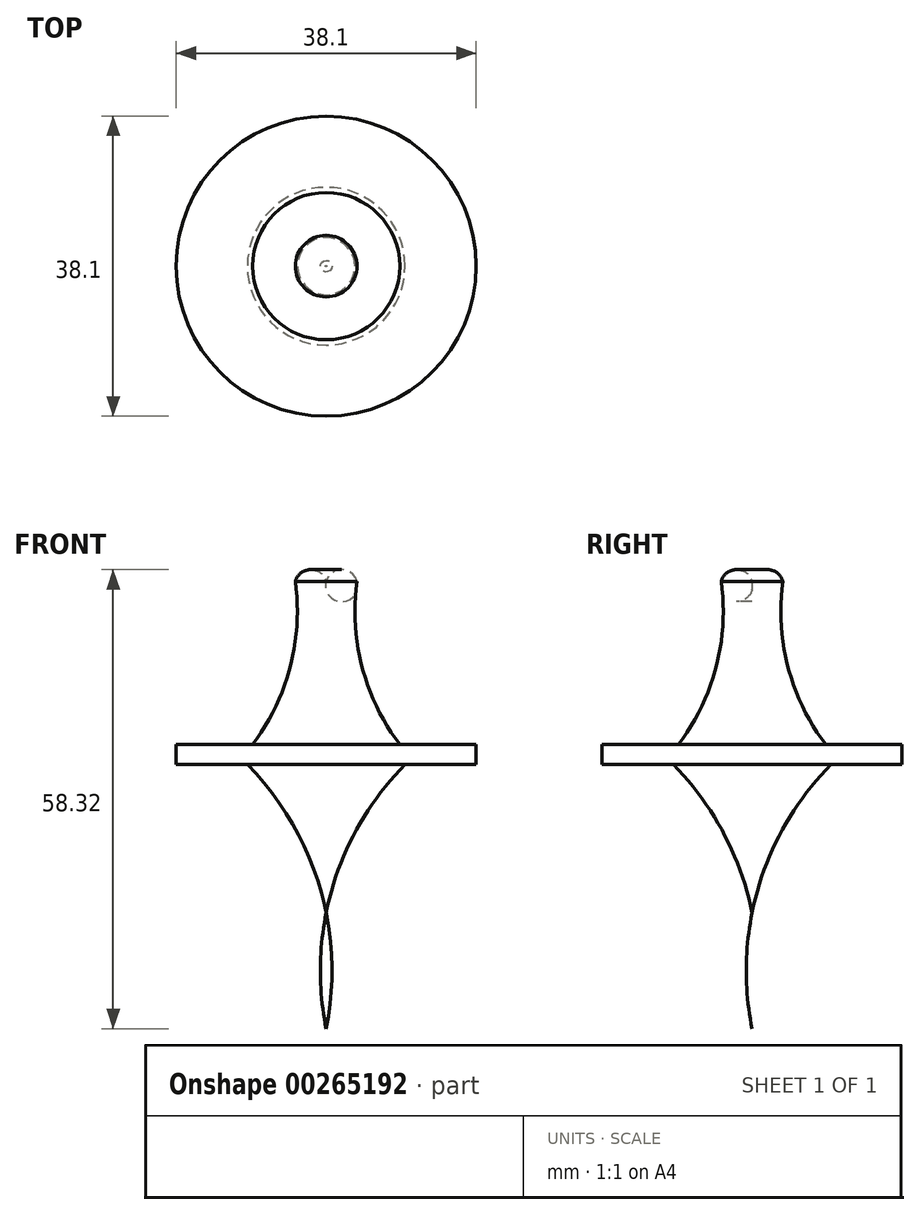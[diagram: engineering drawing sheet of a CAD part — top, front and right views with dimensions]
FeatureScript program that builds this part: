
annotation { "Feature Type Name" : "Feature", "Feature Type Description" : "" }
export const myFeature = defineFeature(function(context is Context, id is Id, definition is map)
    precondition{}
    {
        {
            var Q0;
            Q0=qCreatedBy(makeId("Top.planeOp"),FACE);
            var sketch = newSketch(context, id + "F0", { "sketchPlane" : qUnion([Q0])});
            skCircle(sketch, "E0", {"center": v(0, 0) * mm, "radius": 19.05 * mm});
            skSolve(sketch);
        }
        {
            var Q0;
            Q0=makeQuery(id+"F0.imprint","IMPRINT",FACE,{"disambiguationData":[TD([[makeQuery(id+"F0.imprint","IMPRINT",EDGE,{"derivedFrom":sQuery(id+"F0.wireOp",EDGE,"E0")}),1.0]])]});
            extrude(context, id + "F1", {"entities" : qUnion([Q0]), "depth" : 1.27 * mm});
        }
        {
            var Q0;
            Q0=makeQuery(id+"F1.opExtrude","CAP_FACE",FACE,{"disambiguationData":[OSD([sQuery(id+"F0.wireOp",EDGE,"E0")])],"isStart":true});
            extrude(context, id + "F2", {"entities" : qUnion([Q0]), "operationType" : NewBodyOperationType.ADD, "depth" : 1.27 * mm});
        }
        {
            var Q0;
            Q0=qCreatedBy(makeId("Front.planeOp"),FACE);
            var sketch = newSketch(context, id + "F3", { "sketchPlane" : qUnion([Q0])});
            skArc(sketch, "E1", {"start": v(11.33, 0) * mm, "mid": v(4.07, -9.15) * mm, "end": v(0, -20.1) * mm});
            skLineSegment(sketch, "E2", {"start": v(0, -20.1) * mm, "end": v(0, 0) * mm});
            skLineSegment(sketch, "E3", {"start": v(0, 0) * mm, "end": v(11.33, 0) * mm});
            skSolve(sketch);
        }
        {
            var Q0;
            Q0=makeQuery(id+"F3.imprint","IMPRINT",FACE,{"disambiguationData":[TD([[makeQuery(id+"F3.imprint","IMPRINT",EDGE,{"derivedFrom":sQuery(id+"F3.wireOp",EDGE,"E1")}),-1.0]])]});
            var Q1;
            Q1=sQuery(id+"F3.wireOp",EDGE,"E2");
            revolve(context, id + "F4", {"operationType" : NewBodyOperationType.ADD, "entities" : qUnion([Q0]), "axis" : qUnion([Q1]), "revolveType" : RevolveType.FULL});
        }
        {
            var Q0;
            Q0=qCreatedBy(makeId("Front.planeOp"),FACE);
            var sketch = newSketch(context, id + "F5", { "sketchPlane" : qUnion([Q0])});
            skArc(sketch, "E4", {"start": v(3.91, 22.01) * mm, "mid": v(4.8, 10.32) * mm, "end": v(10.37, 0) * mm});
            skArc(sketch, "E5", {"start": v(3.91, 22.01) * mm, "mid": v(1.96, 23.5) * mm, "end": v(0, 22.01) * mm});
            skLineSegment(sketch, "E6", {"start": v(0, 22.01) * mm, "end": v(0, 0) * mm});
            skLineSegment(sketch, "E7", {"start": v(10.37, 0) * mm, "end": v(0, 0) * mm});
            skSolve(sketch);
        }
        {
            var Q0;
            Q0=makeQuery(id+"F5.imprint","IMPRINT",FACE,{"disambiguationData":[TD([[makeQuery(id+"F5.imprint","IMPRINT",EDGE,{"derivedFrom":sQuery(id+"F5.wireOp",EDGE,"E4")}),-1.0]])]});
            var Q1;
            Q1=sQuery(id+"F5.wireOp",EDGE,"E6");
            revolve(context, id + "F6", {"operationType" : NewBodyOperationType.ADD, "entities" : qUnion([Q0]), "axis" : qUnion([Q1]), "revolveType" : RevolveType.FULL});
        }
    });
